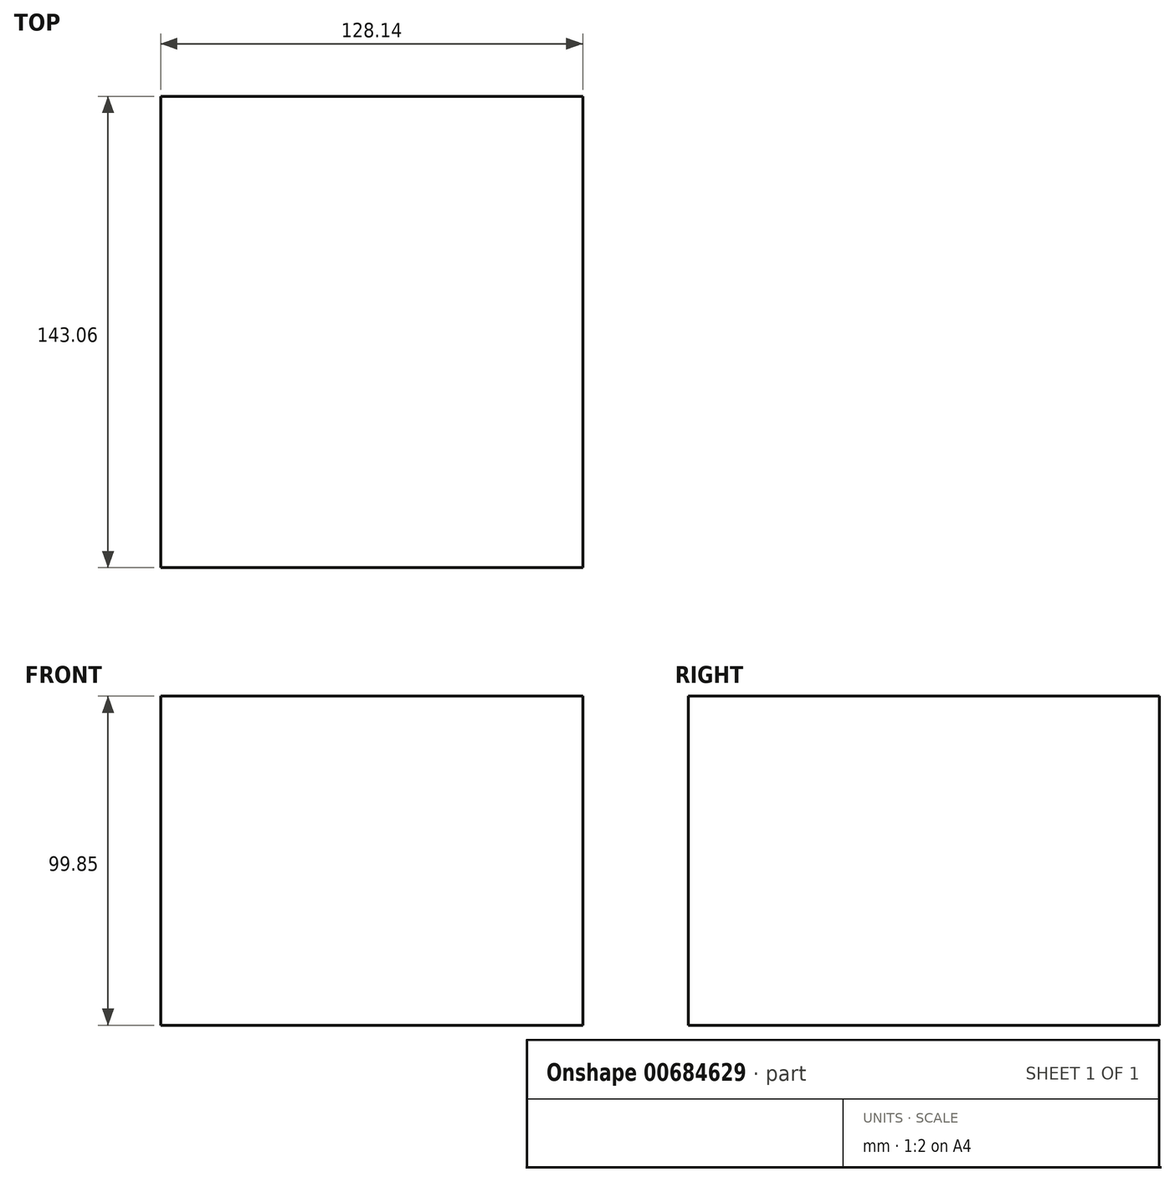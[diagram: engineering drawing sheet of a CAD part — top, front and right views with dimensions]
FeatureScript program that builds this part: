
annotation { "Feature Type Name" : "Feature", "Feature Type Description" : "" }
export const myFeature = defineFeature(function(context is Context, id is Id, definition is map)
    precondition{}
    {
        {
            var Q0;
            Q0=qCreatedBy(makeId("Top.planeOp"),FACE);
            var sketch = newSketch(context, id + "F0", { "sketchPlane" : qUnion([Q0])});
            skLineSegment(sketch, "E0.bottom", {"start": v(0, 0) * mm, "end": v(128.14, 0) * mm});
            skLineSegment(sketch, "E0.top", {"start": v(0, -143.06) * mm, "end": v(128.14, -143.06) * mm});
            skLineSegment(sketch, "E0.left", {"start": v(0, 0) * mm, "end": v(0, -143.06) * mm});
            skLineSegment(sketch, "E0.right", {"start": v(128.14, 0) * mm, "end": v(128.14, -143.06) * mm});
            skSolve(sketch);
        }
        {
            var Q0;
            Q0=makeQuery(id+"F0.imprint","IMPRINT",FACE,{"disambiguationData":[TD([[makeQuery(id+"F0.imprint","IMPRINT",EDGE,{"derivedFrom":sQuery(id+"F0.wireOp",EDGE,"E0.bottom")}),-1.0]])]});
            extrude(context, id + "F1", {"entities" : qUnion([Q0]), "depth" : 99.85 * mm, "offsetDistance" : 25.4 * mm});
        }
    });
